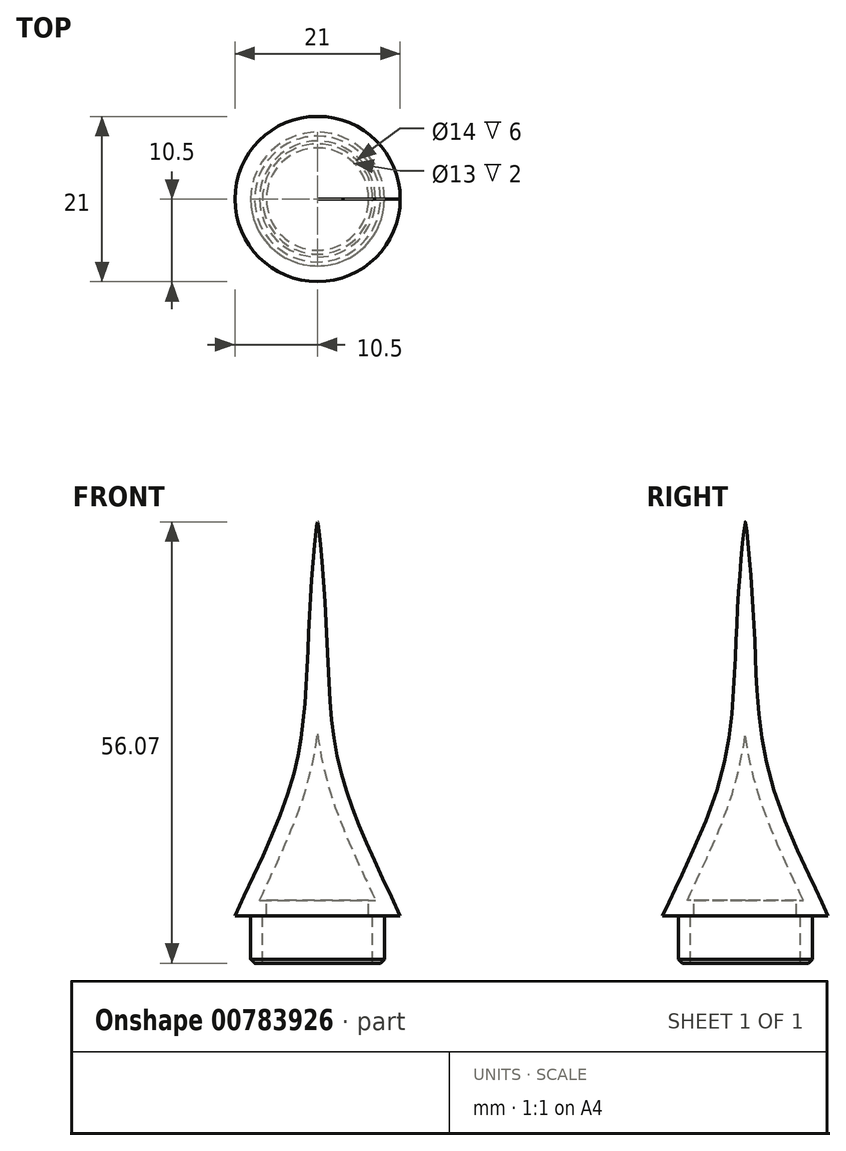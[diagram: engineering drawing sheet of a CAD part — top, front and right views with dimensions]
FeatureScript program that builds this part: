
annotation { "Feature Type Name" : "Feature", "Feature Type Description" : "" }
export const myFeature = defineFeature(function(context is Context, id is Id, definition is map)
    precondition{}
    {
        {
            var Q0;
            Q0=qCreatedBy(makeId("Front.planeOp"),FACE);
            var sketch = newSketch(context, id + "F0", { "sketchPlane" : qUnion([Q0])});
            skLineSegment(sketch, "E0", {"start": v(0, 0) * mm, "end": v(0, 50) * mm});
            skLineSegment(sketch, "E1", {"start": v(10.5, 0) * mm, "end": v(0, 0) * mm});
            skFitSpline(sketch, "E2", {"points": [v(0, 50) * mm, v(0.93, 40.17) * mm, v(2.73, 19.24) * mm, v(10.5, 0) * mm], "startDerivative": vector(0, 8.62) * mm, "endDerivative": vector(26.2, -57.18) * mm});
            skSolve(sketch);
        }
        {
            var Q0;
            Q0=makeQuery(id+"F0.imprint","IMPRINT",FACE,{"disambiguationData":[TD([[makeQuery(id+"F0.imprint","IMPRINT",EDGE,{"derivedFrom":sQuery(id+"F0.wireOp",EDGE,"E0")}),-1.0]])]});
            var Q1;
            Q1=sQuery(id+"F0.wireOp",EDGE,"E0");
            revolve(context, id + "F1", {"surfaceOperationType" : NewSurfaceOperationType.NEW, "entities" : qUnion([Q0]), "axis" : qUnion([Q1]), "revolveType" : RevolveType.FULL});
        }
        {
            var Q0;
            Q0=makeQuery(id+"F1.opRevolve","SWEPT_FACE",FACE,{"disambiguationData":[OSD([sQuery(id+"F0.wireOp",EDGE,"E1")])]});
            var sketch = newSketch(context, id + "F2", { "sketchPlane" : qUnion([Q0])});
            skCircle(sketch, "E3", {"center": v(0, 0) * mm, "radius": 8.5 * mm});
            skCircle(sketch, "E4", {"center": v(0, 0) * mm, "radius": 7 * mm});
            skSolve(sketch);
        }
        {
            var Q0;
            Q0=makeQuery(id+"F2.imprint","IMPRINT",FACE,{"disambiguationData":[TD([[makeQuery(id+"F2.imprint","IMPRINT",EDGE,{"derivedFrom":sQuery(id+"F2.wireOp",EDGE,"E3")}),1.0]])]});
            extrude(context, id + "F3", {"entities" : qUnion([Q0]), "operationType" : NewBodyOperationType.ADD, "depth" : 6 * mm, "offsetDistance" : 25.4 * mm});
        }
        {
            var Q0;
            Q0=makeQuery(id+"F3.opExtrude","CAP_EDGE",EDGE,{"disambiguationData":[OSD([sQuery(id+"F2.wireOp",EDGE,"E3")])],"isStart":false});
            chamfer(context, id + "F4", {"entities" : qUnion([Q0]), "width" : .5 * mm, "tangentPropagation" : true});
        }
        {
            var Q0;
            Q0=makeQuery(id+"F3.boolean.opBoolean","SPLIT",FACE,{"disambiguationData":[TD([makeQuery(id+"F3.opExtrude","SWEPT_FACE",FACE,{"disambiguationData":[OSD([sQuery(id+"F2.wireOp",EDGE,"E4")])]})])],"derivedFrom":makeQuery(id+"F1.opRevolve","SWEPT_FACE",FACE,{"disambiguationData":[OSD([sQuery(id+"F0.wireOp",EDGE,"E1")])]})});
            shell(context, id + "F5", {"entities" : qUnion([Q0]), "thickness" : 2 * mm});
        }
    });
